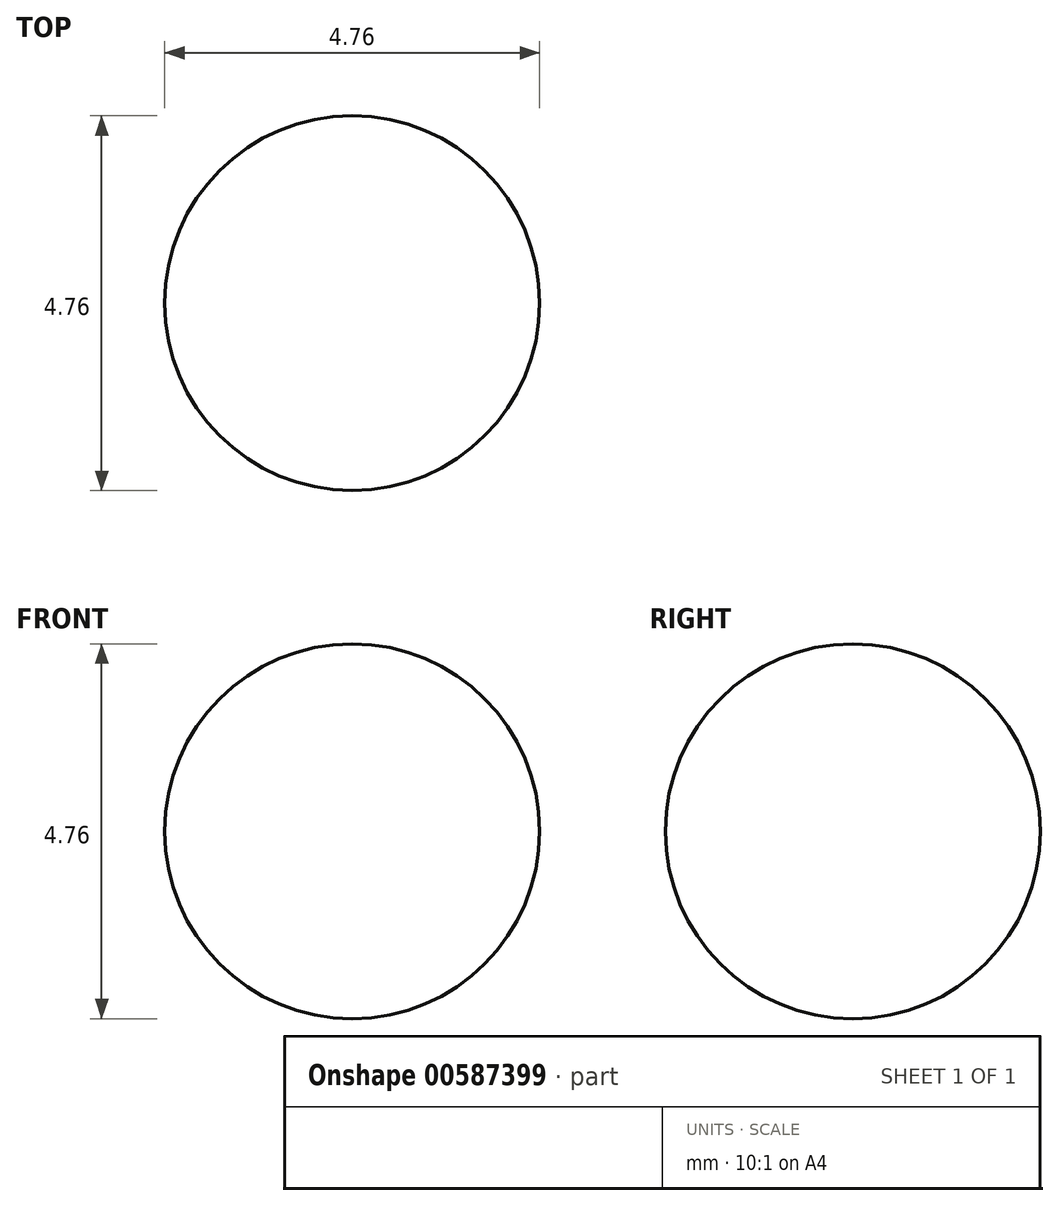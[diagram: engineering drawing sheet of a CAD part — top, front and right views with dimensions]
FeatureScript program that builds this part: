
annotation { "Feature Type Name" : "Feature", "Feature Type Description" : "" }
export const myFeature = defineFeature(function(context is Context, id is Id, definition is map)
    precondition{}
    {
        {
            var Q0;
            Q0=qCreatedBy(makeId("Front.planeOp"),FACE);
            var sketch = newSketch(context, id + "F0", { "sketchPlane" : qUnion([Q0])});
            skLineSegment(sketch, "E0", {"start": v(4.5, 0) * mm, "end": v(-5.27, 0) * mm, "construction": true});
            skArc(sketch, "E1", {"start": v(2.38, 0) * mm, "mid": v(0, 2.38) * mm, "end": v(-2.38, 0) * mm});
            skLineSegment(sketch, "E2", {"start": v(-2.38, 0) * mm, "end": v(2.38, 0) * mm});
            skSolve(sketch);
        }
        {
            var Q0;
            Q0=makeQuery(id+"F0.imprint","IMPRINT",FACE,{"disambiguationData":[TD([[makeQuery(id+"F0.imprint","IMPRINT",EDGE,{"derivedFrom":sQuery(id+"F0.wireOp",EDGE,"E1")}),1.0]])]});
            var Q1;
            Q1=sQuery(id+"F0.wireOp",EDGE,"E2");
            revolve(context, id + "F1", {"entities" : qUnion([Q0]), "axis" : qUnion([Q1]), "revolveType" : RevolveType.FULL});
        }
    });
